# Revit family: 6DMLH-NRG
name_source: partatom
category: Mechanical Equipment
units: mm (PartAtom-declared; Revit-internal decimal feet)

## family parameters
Always vertical = Yes
Cut with Voids When Loaded = No
OmniClass Number = 23.40.40.11.17
OmniClass Title = Refrigerated Cases
Part Type = Normal
Room Calculation Point = No
Round Connector Dimension = Use Radius
Shared = No
Work Plane-Based = Yes

## types (12) — shared parameters
24" Shelf = Yes
BOTTOM ELECTRICAL = Yes
BOTTOM REFRIGERATION PIPING = Yes
Certifications = NSF 7, UL471, CSA
DATE = 04/29/2016
DRAIN PIPING = Yes
Default Elevation = 48"
Description = High Multi-Deck Merchandiser with Synerg-E™
Discharge Air Velocity (FPM) = 260 FPM
EQUIPMENT DESCRIPTION = High Multi-Deck Merchandiser with Synerg-E™
EQUIPMENT MARK = 6DMLH-NRG
GLASS = Glass
Height = 88 5/8"
Item Description = High Multi-Deck Merchandiser with Synerg-E™
Legend Number = 6DMLH-NRG
Manufacturer = HILL PHOENIX
Model = 6DMLH-NRG
PAINTED METAL UPPER SHELF = PAINTED SHELVES
REFRIGERATION PIPING = COPPER PIPE
SOLID STD LH END = Yes
SOLID STD RH END = Yes
STAINLESS STEEL = GALVANIZED STEEL
Standard Power Amps = 0 A
Superheat Set Point @ Bulb (°F) = 6-8 °F
TOP ELECTRICAL = Yes
TOP REFRIGERATION PIPING = Yes
Timed-Off Defrost Termination Temp = 42 °F
URL = http://www.hillphoenix.com
Width = 42 3/4"

## per-type parameters (varying)
- 04' Dairy/Deli/Cut Produce: Application Discipline=Bulk Produce/Beverage; BTUH Conventional=1545; BTUH Parallel=1475; DRAIN LINE=24"; Defrosts Per Day=2; Discharge Air (°F)=37 °F; Evaporator (°F)=34 °F; FULL VIEW LH END=Yes; FULL VIEW RH END=Yes; High Efficiency Amps=1 A; High Efficiency Watts=65 W; High Power (Cornice) Amps=1 A; High Power (Cornice) Watts=65 W; KP LH=No; KP RH=No; LF STD END=Yes; Length=48"; Length of Cases=48"; Light Length=3'; Lights Per Row=2; Number of Fans=3; REDUCED RH END=Yes; REDUCED VIEW LH END=Yes; RT STD END=Yes; SOLID EXT LH END=Yes; SOLID EXT RH END=Yes; SQUARE END LH=Yes; SQUARE END RH=Yes; SUPER VIEW LH END=Yes; SUPER VIEW RH END=Yes; Standard Power Watts=36 W; Timed-Off Defrost Fail-Safe (Min)=30 (min)
- 06' Dairy/Deli/Cut Produce: Application Discipline=Dairy/Deli/Cut Produce; BTUH Conventional=1756; BTUH Parallel=1500; DRAIN LINE=36"; Defrosts Per Day=6; Discharge Air (°F)=34 °F; Evaporator (°F)=25 °F; FULL VIEW LH END=Yes; FULL VIEW RH END=Yes; High Efficiency Amps=1 A; High Efficiency Watts=65 W; High Power (Cornice) Amps=0 A; High Power (Cornice) Watts=30 W; KP LH=No; KP RH=No; LF STD END=Yes; Length=72"; Length of Cases=72"; Light Length=3'; Lights Per Row=2; Number of Fans=3; REDUCED RH END=Yes; REDUCED VIEW LH END=Yes; RT STD END=Yes; SOLID EXT LH END=Yes; SOLID EXT RH END=Yes; SQUARE END LH=Yes; SQUARE END RH=Yes; SUPER VIEW LH END=Yes; SUPER VIEW RH END=Yes; Standard Power Watts=17 W; Timed-Off Defrost Fail-Safe (Min)=45 (min)
- 08' Dairy/Deli/Cut Produce: Application Discipline=Dairy/Deli/Cut Produce; BTUH Conventional=1756; BTUH Parallel=1500; DRAIN LINE=48"; Defrosts Per Day=6; Discharge Air (°F)=34 °F; Evaporator (°F)=25 °F; FULL VIEW LH END=Yes; FULL VIEW RH END=Yes; High Efficiency Amps=1 A; High Efficiency Watts=65 W; High Power (Cornice) Amps=0 A; High Power (Cornice) Watts=43 W; KP LH=No; KP RH=No; LF STD END=Yes; Length=96"; Length of Cases=96"; Light Length=4'; Lights Per Row=2; Number of Fans=3; REDUCED RH END=Yes; REDUCED VIEW LH END=Yes; RT STD END=Yes; SOLID EXT LH END=Yes; SOLID EXT RH END=Yes; SQUARE END LH=Yes; SQUARE END RH=Yes; SUPER VIEW LH END=Yes; SUPER VIEW RH END=Yes; Standard Power Watts=24 W; Timed-Off Defrost Fail-Safe (Min)=45 (min)
- 12' Dairy/Deli/Cut Produce: Application Discipline=Dairy/Deli/Cut Produce; BTUH Conventional=1756; BTUH Parallel=1500; DRAIN LINE=72"; Defrosts Per Day=6; Discharge Air (°F)=34 °F; Evaporator (°F)=25 °F; FULL VIEW LH END=Yes; FULL VIEW RH END=Yes; High Efficiency Amps=1 A; High Efficiency Watts=87 W; High Power (Cornice) Amps=1 A; High Power (Cornice) Watts=65 W; KP LH=No; KP RH=No; LF STD END=Yes; Length=144"; Length of Cases=144"; Light Length=4'; Lights Per Row=3; Number of Fans=4; REDUCED RH END=Yes; REDUCED VIEW LH END=Yes; RT STD END=Yes; SOLID EXT LH END=Yes; SOLID EXT RH END=Yes; SQUARE END LH=Yes; SQUARE END RH=Yes; SUPER VIEW LH END=Yes; SUPER VIEW RH END=Yes; Standard Power Watts=36 W; Timed-Off Defrost Fail-Safe (Min)=45 (min)
- 04' Bulk Produce/Beverage: Application Discipline=Bulk Produce/Beverage; BTUH Conventional=1756; BTUH Parallel=1500; DRAIN LINE=24"; Defrosts Per Day=6; Discharge Air (°F)=34 °F; Evaporator (°F)=25 °F; FULL VIEW LH END=Yes; FULL VIEW RH END=Yes; High Efficiency Amps=0 A; High Efficiency Watts=43 W; High Power (Cornice) Amps=0 A; High Power (Cornice) Watts=22 W; KP LH=No; KP RH=No; LF STD END=Yes; Length=48"; Length of Cases=48"; Light Length=4'; Lights Per Row=1; Number of Fans=2; REDUCED RH END=Yes; REDUCED VIEW LH END=Yes; RT STD END=Yes; SOLID EXT LH END=Yes; SOLID EXT RH END=Yes; SQUARE END LH=Yes; SQUARE END RH=Yes; SUPER VIEW LH END=Yes; SUPER VIEW RH END=Yes; Standard Power Watts=12 W; Timed-Off Defrost Fail-Safe (Min)=45 (min)
- 06' Bulk Produce/Beverage: Application Discipline=Bulk Produce/Beverage; BTUH Conventional=1756; BTUH Parallel=1500; DRAIN LINE=36"; Defrosts Per Day=6; Discharge Air (°F)=34 °F; Evaporator (°F)=25 °F; FULL VIEW LH END=Yes; FULL VIEW RH END=Yes; High Efficiency Amps=1 A; High Efficiency Watts=65 W; High Power (Cornice) Amps=0 A; High Power (Cornice) Watts=30 W; KP LH=No; KP RH=No; LF STD END=Yes; Length=72"; Length of Cases=72"; Light Length=3'; Lights Per Row=2; Number of Fans=3; REDUCED RH END=Yes; REDUCED VIEW LH END=Yes; RT STD END=Yes; SOLID EXT LH END=Yes; SOLID EXT RH END=Yes; SQUARE END LH=Yes; SQUARE END RH=Yes; SUPER VIEW LH END=Yes; SUPER VIEW RH END=Yes; Standard Power Watts=17 W; Timed-Off Defrost Fail-Safe (Min)=45 (min)
- 08' Bulk Produce/Beverage: Application Discipline=Bulk Produce/Beverage; BTUH Conventional=1756; BTUH Parallel=1500; DRAIN LINE=48"; Defrosts Per Day=6; Discharge Air (°F)=34 °F; Evaporator (°F)=25 °F; FULL VIEW LH END=Yes; FULL VIEW RH END=Yes; High Efficiency Amps=1 A; High Efficiency Watts=65 W; High Power (Cornice) Amps=0 A; High Power (Cornice) Watts=43 W; KP LH=No; KP RH=No; LF STD END=Yes; Length=96"; Length of Cases=96"; Light Length=4'; Lights Per Row=2; Number of Fans=3; REDUCED RH END=Yes; REDUCED VIEW LH END=Yes; RT STD END=Yes; SOLID EXT LH END=Yes; SOLID EXT RH END=Yes; SQUARE END LH=Yes; SQUARE END RH=Yes; SUPER VIEW LH END=Yes; SUPER VIEW RH END=Yes; Standard Power Watts=24 W; Timed-Off Defrost Fail-Safe (Min)=45 (min)
- 12' Bulk Produce/Beverage: Application Discipline=Bulk Produce/Beverage; BTUH Conventional=1756; BTUH Parallel=1500; DRAIN LINE=72"; Defrosts Per Day=6; Discharge Air (°F)=34 °F; Evaporator (°F)=25 °F; FULL VIEW LH END=No; FULL VIEW RH END=No; High Efficiency Amps=1 A; High Efficiency Watts=87 W; High Power (Cornice) Amps=1 A; High Power (Cornice) Watts=65 W; KP LH=Yes; KP RH=Yes; LF STD END=No; Length=144"; Length of Cases=144"; Light Length=4'; Lights Per Row=3; Number of Fans=4; REDUCED RH END=No; REDUCED VIEW LH END=No; RT STD END=No; SOLID EXT LH END=No; SOLID EXT RH END=No; SQUARE END LH=No; SQUARE END RH=No; SUPER VIEW LH END=No; SUPER VIEW RH END=No; Standard Power Watts=36 W; Timed-Off Defrost Fail-Safe (Min)=45 (min)
- 12': Application Discipline=Bulk Produce/Beverage; BTUH Conventional=1756; BTUH Parallel=1500; DRAIN LINE=72"; Defrosts Per Day=6; Discharge Air (°F)=34 °F; Evaporator (°F)=25 °F; FULL VIEW LH END=No; FULL VIEW RH END=No; High Efficiency Amps=1 A; High Efficiency Watts=87 W; High Power (Cornice) Amps=1 A; High Power (Cornice) Watts=65 W; KP LH=Yes; KP RH=Yes; LF STD END=No; Length=144"; Length of Cases=144"; Light Length=4'; Lights Per Row=3; Number of Fans=4; REDUCED RH END=No; REDUCED VIEW LH END=No; RT STD END=No; SOLID EXT LH END=No; SOLID EXT RH END=No; SQUARE END LH=No; SQUARE END RH=No; SUPER VIEW LH END=No; SUPER VIEW RH END=No; Standard Power Watts=36 W; Timed-Off Defrost Fail-Safe (Min)=45 (min)
- 8': Application Discipline=Bulk Produce/Beverage; BTUH Conventional=1756; BTUH Parallel=1500; DRAIN LINE=48"; Defrosts Per Day=6; Discharge Air (°F)=34 °F; Evaporator (°F)=25 °F; FULL VIEW LH END=Yes; FULL VIEW RH END=Yes; High Efficiency Amps=1 A; High Efficiency Watts=65 W; High Power (Cornice) Amps=1 A; High Power (Cornice) Watts=65 W; KP LH=No; KP RH=No; LF STD END=No; Length=96"; Length of Cases=144"; Light Length=4'; Lights Per Row=2; Number of Fans=3; REDUCED RH END=Yes; REDUCED VIEW LH END=Yes; RT STD END=No; SOLID EXT LH END=Yes; SOLID EXT RH END=Yes; SQUARE END LH=Yes; SQUARE END RH=Yes; SUPER VIEW LH END=Yes; SUPER VIEW RH END=Yes; Standard Power Watts=36 W; Timed-Off Defrost Fail-Safe (Min)=45 (min)
- 6': Application Discipline=Bulk Produce/Beverage; BTUH Conventional=1545; BTUH Parallel=1475; DRAIN LINE=36"; Defrosts Per Day=2; Discharge Air (°F)=37 °F; Evaporator (°F)=34 °F; FULL VIEW LH END=Yes; FULL VIEW RH END=Yes; High Efficiency Amps=1 A; High Efficiency Watts=65 W; High Power (Cornice) Amps=1 A; High Power (Cornice) Watts=65 W; KP LH=No; KP RH=No; LF STD END=Yes; Length=72"; Length of Cases=144"; Light Length=3'; Lights Per Row=2; Number of Fans=3; REDUCED RH END=Yes; REDUCED VIEW LH END=Yes; RT STD END=Yes; SOLID EXT LH END=Yes; SOLID EXT RH END=Yes; SQUARE END LH=Yes; SQUARE END RH=Yes; SUPER VIEW LH END=Yes; SUPER VIEW RH END=Yes; Standard Power Watts=36 W; Timed-Off Defrost Fail-Safe (Min)=30
- 4': Application Discipline=Dairy/Deli/Cut Produce; BTUH Conventional=1695; BTUH Parallel=1585; DRAIN LINE=24"; Defrosts Per Day=6; Discharge Air (°F)=31 °F; Evaporator (°F)=28 °F; FULL VIEW LH END=Yes; FULL VIEW RH END=Yes; High Efficiency Amps=0 A; High Efficiency Watts=43 W; High Power (Cornice) Amps=1 A; High Power (Cornice) Watts=65 W; KP LH=No; KP RH=No; LF STD END=Yes; Length=48"; Length of Cases=144"; Light Length=4'; Lights Per Row=1; Number of Fans=2; REDUCED RH END=Yes; REDUCED VIEW LH END=Yes; RT STD END=Yes; SOLID EXT LH END=Yes; SOLID EXT RH END=Yes; SQUARE END LH=Yes; SQUARE END RH=Yes; SUPER VIEW LH END=Yes; SUPER VIEW RH END=Yes; Standard Power Watts=36 W; Timed-Off Defrost Fail-Safe (Min)=45

## geometry (parser evidence)
native form markers: Blend x38, Sweep x13
no freeform markers — native parametric forms only
